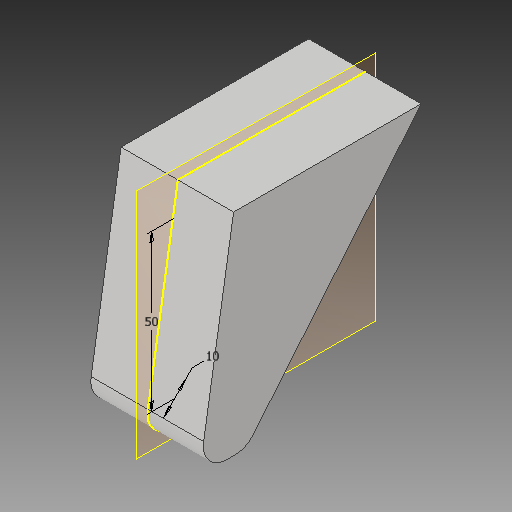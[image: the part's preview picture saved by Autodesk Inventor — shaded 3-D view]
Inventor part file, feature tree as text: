
AUTODESK INVENTOR PART (.ipt)
format: ipt  version: 2019 (Build 230136000, 136)  size: 114,688 bytes
history: native  units: mm
features: other x2, sketch x2, extrude x1, projected_geometry x1
ambient origin geometry x8: Origin, YZ Plane, XZ Plane, XY Plane, X Axis, Y Axis, Z Axis, Center Point
bodies: Body1 (feature_tree)
feature tree (6):
  other  "솔리드1"
  extrude  "돌출1"  Depth=67.5mm
  other  "작업 평면1"
  sketch  "스케치2"
  sketch  "스케치1"
  projected_geometry  "투영된 루프1"
